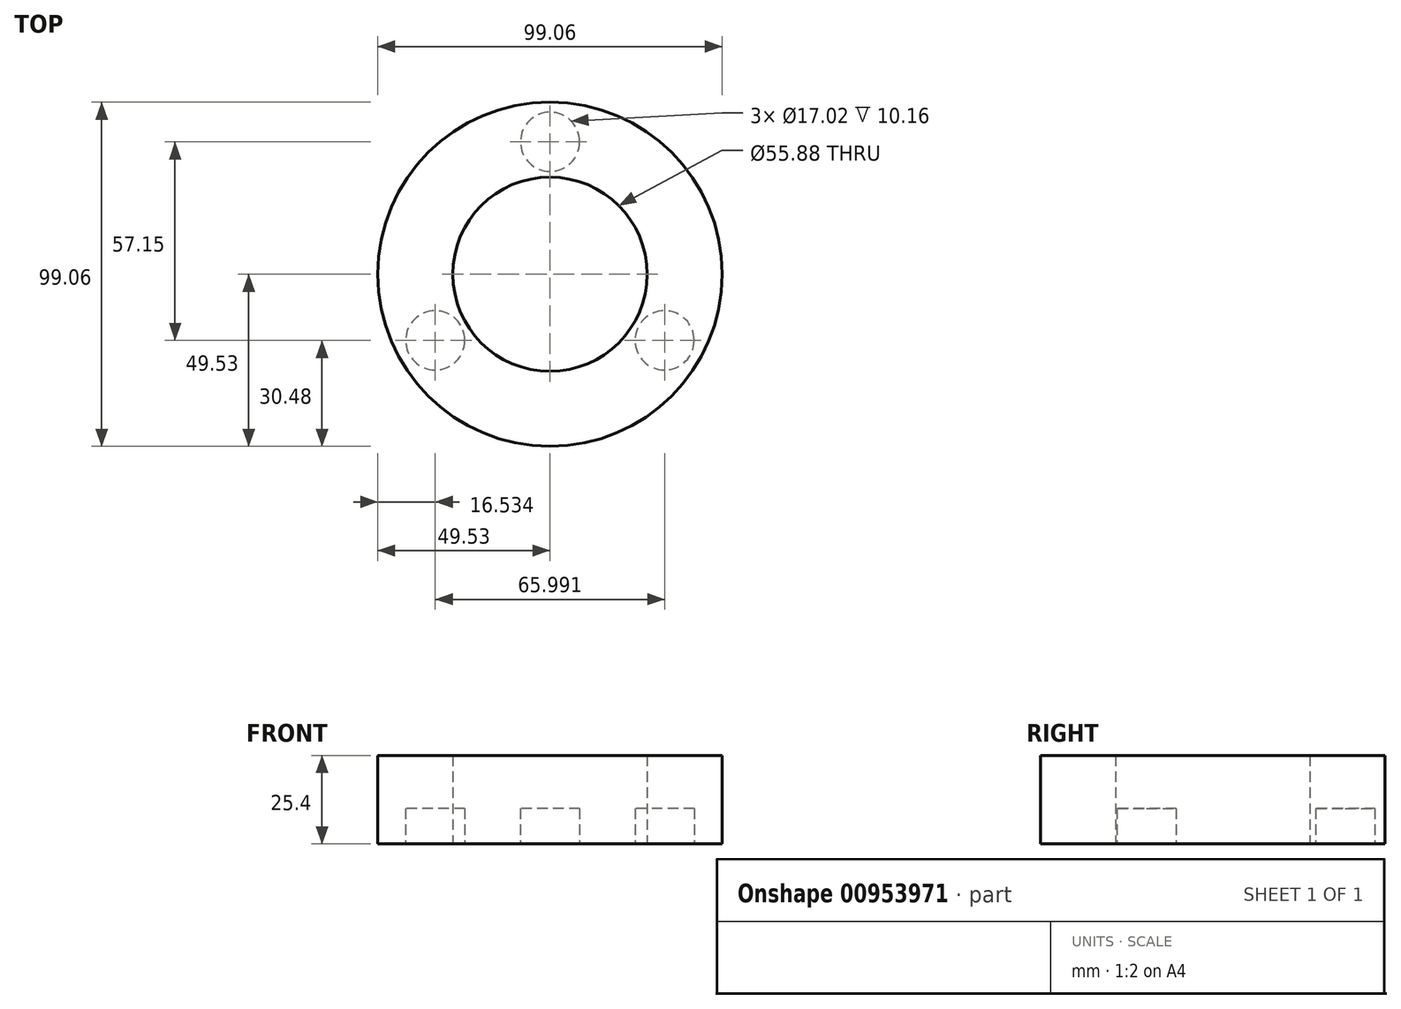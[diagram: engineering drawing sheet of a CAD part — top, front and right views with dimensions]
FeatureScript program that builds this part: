
annotation { "Feature Type Name" : "Feature", "Feature Type Description" : "" }
export const myFeature = defineFeature(function(context is Context, id is Id, definition is map)
    precondition{}
    {
        {
            var Q0;
            Q0=qCreatedBy(makeId("Top.planeOp"),FACE);
            var sketch = newSketch(context, id + "F0", { "sketchPlane" : qUnion([Q0])});
            skCircle(sketch, "E0", {"center": v(0, 0) * mm, "radius": 49.53 * mm});
            skCircle(sketch, "E1", {"center": v(0, 0) * mm, "radius": 27.94 * mm});
            skCircle(sketch, "E2", {"center": v(0.02, 38.1) * mm, "radius": 8.5 * mm});
            skCircle(sketch, "E3", {"center": v(33, -19.05) * mm, "radius": 8.5 * mm});
            skCircle(sketch, "E4", {"center": v(-33, -19.05) * mm, "radius": 8.5 * mm});
            skSolve(sketch);
        }
        {
            var Q0;
            Q0=makeQuery(id+"F0.imprint","IMPRINT",FACE,{"disambiguationData":[TD([[makeQuery(id+"F0.imprint","IMPRINT",EDGE,{"derivedFrom":sQuery(id+"F0.wireOp",EDGE,"E0")}),1.0]])]});
            var Q1;
            Q1=makeQuery(id+"F0.imprint","IMPRINT",FACE,{"disambiguationData":[TD([[makeQuery(id+"F0.imprint","IMPRINT",EDGE,{"derivedFrom":sQuery(id+"F0.wireOp",EDGE,"E2")}),1.0]])]});
            var Q2;
            Q2=makeQuery(id+"F0.imprint","IMPRINT",FACE,{"disambiguationData":[TD([[makeQuery(id+"F0.imprint","IMPRINT",EDGE,{"derivedFrom":sQuery(id+"F0.wireOp",EDGE,"E4")}),1.0]])]});
            var Q3;
            Q3=makeQuery(id+"F0.imprint","IMPRINT",FACE,{"disambiguationData":[TD([[makeQuery(id+"F0.imprint","IMPRINT",EDGE,{"derivedFrom":sQuery(id+"F0.wireOp",EDGE,"E3")}),1.0]])]});
            extrude(context, id + "F1", {"entities" : qUnion([Q0, Q1, Q2, Q3]), "depth" : 25.4 * mm, "offsetDistance" : 25.4 * mm});
        }
        {
            var Q0;
            Q0=makeQuery(id+"F1.opExtrude","CAP_FACE",FACE,{"disambiguationData":[OSD([sQuery(id+"F0.wireOp",EDGE,"E0"),sQuery(id+"F0.wireOp",EDGE,"E1"),sQuery(id+"F0.wireOp",EDGE,"sREMWjoi-2Ct3-MFz1-rjZK-BklZlzJ07p4H"),sQuery(id+"F0.wireOp",EDGE,"5ov9ko90-olbK-U4Jc-B4Gc-dOT4fDAnR858")])],"isStart":false});
            var Q1;
            Q1=makeQuery(id+"F0.imprint","IMPRINT",FACE,{"disambiguationData":[TD([[makeQuery(id+"F0.imprint","IMPRINT",EDGE,{"derivedFrom":sQuery(id+"F0.wireOp",EDGE,"E2")}),1.0]])]});
            var Q2;
            Q2=makeQuery(id+"F0.imprint","IMPRINT",FACE,{"disambiguationData":[TD([[makeQuery(id+"F0.imprint","IMPRINT",EDGE,{"derivedFrom":sQuery(id+"F0.wireOp",EDGE,"E4")}),1.0]])]});
            var Q3;
            Q3=makeQuery(id+"F0.imprint","IMPRINT",FACE,{"disambiguationData":[TD([[makeQuery(id+"F0.imprint","IMPRINT",EDGE,{"derivedFrom":sQuery(id+"F0.wireOp",EDGE,"E3")}),1.0]])]});
            extrude(context, id + "F2", {"entities" : qUnion([Q0, Q1, Q2, Q3]), "operationType" : NewBodyOperationType.REMOVE, "depth" : 10.16 * mm, "offsetDistance" : 25.4 * mm});
        }
    });
